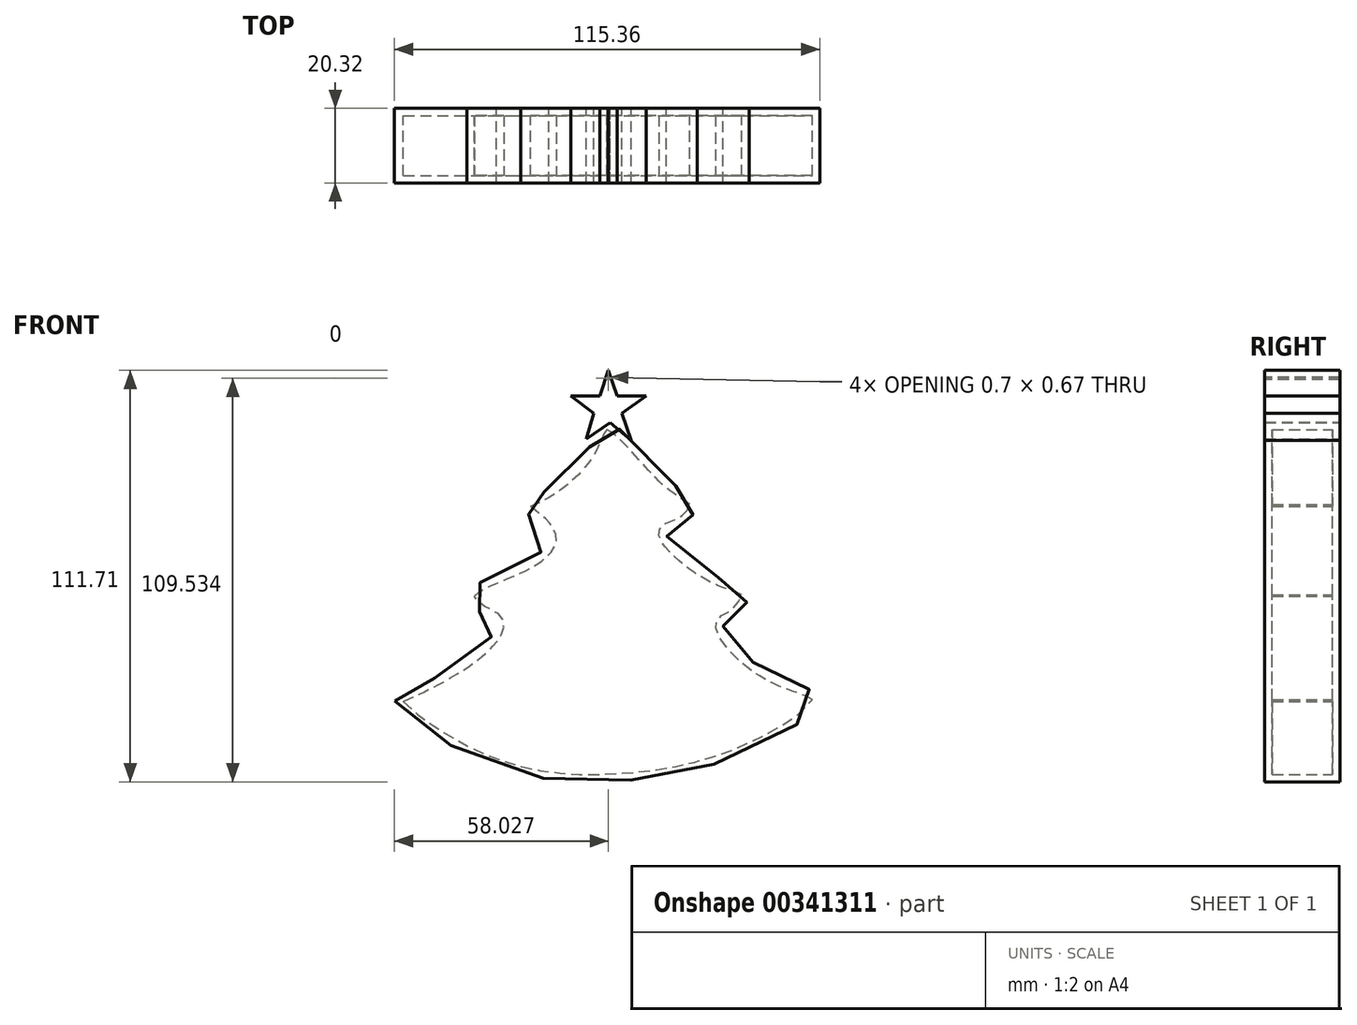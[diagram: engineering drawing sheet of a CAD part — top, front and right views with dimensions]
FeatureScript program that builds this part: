
annotation { "Feature Type Name" : "Feature", "Feature Type Description" : "" }
export const myFeature = defineFeature(function(context is Context, id is Id, definition is map)
    precondition{}
    {
        {
            var Q0;
            Q0=qCreatedBy(makeId("Front.planeOp"),FACE);
            var sketch = newSketch(context, id + "F0", { "sketchPlane" : qUnion([Q0])});
            skPoint(sketch, "E0.15.internal.snap0", {"position": v(1.13, 56.39) * mm});
            skFitSpline(sketch, "E0", {"points": [v(-56.53, -29.1) * mm, v(-32.06, -45.7) * mm, v(5.35, -50.76) * mm, v(39.1, -42.89) * mm, v(58.79, -28.54) * mm, v(48.38, -23.2) * mm, v(35.16, -13.36) * mm, v(32.63, -8.3) * mm, v(35.16, -6.6) * mm, v(39.66, 0) * mm, v(30.1, 4.92) * mm, v(17.16, 16.45) * mm, v(20.82, 18.42) * mm, v(25.6, 24.33) * mm, v(18.85, 29.95) * mm, v(1.13, 46.54) * mm, v(-4.21, 38.67) * mm, v(-18, 26.58) * mm, v(-22.21, 23.76) * mm, v(-14.9, 16.17) * mm, v(-21.93, 8.02) * mm, v(-36.84, 0) * mm, v(-33.46, -4.92) * mm, v(-28.96, -8.02) * mm, v(-34.87, -16.17) * mm, v(-54.28, -27.14) * mm, v(-56.53, -29.1) * mm]});
            skSolve(sketch);
        }
        {
            var Q0;
            Q0 = qSketchRegion(id + "F0", true);
            extrude(context, id + "F1", {"entities" : qUnion([Q0]), "depth" : 20.32 * mm});
        }
        {
            var Q0;
            Q0=makeQuery(id+"F1.opExtrude","CAP_FACE",FACE,{"disambiguationData":[OSD([sQuery(id+"F0.wireOp",EDGE,"E0")])],"isStart":false});
            var Q1;
            Q1=makeQuery(id+"F1.opExtrude","SWEPT_BODY",BODY,{"disambiguationData":[OSD([sQuery(id+"F0.wireOp",EDGE,"E0")])]});
            shell(context, id + "F2", {"isHollow" : true, "entities" : qUnion([Q0]), "parts" : qUnion([Q1]), "thickness" : 2 * mm});
        }
        {
            var Q0;
            Q0=makeQuery(id+"F1.opExtrude","CAP_FACE",FACE,{"disambiguationData":[OSD([sQuery(id+"F0.wireOp",EDGE,"E0")])],"isStart":false});
            var sketch = newSketch(context, id + "F3", { "sketchPlane" : qUnion([Q0])});
            skLineSegment(sketch, "E1", {"start": v(-8.68, 53.61) * mm, "end": v(-0.89, 53.61) * mm});
            skLineSegment(sketch, "E2", {"start": v(-0.89, 53.61) * mm, "end": v(1.45, 60.62) * mm});
            skLineSegment(sketch, "E3", {"start": v(1.45, 60.62) * mm, "end": v(3.86, 53.7) * mm});
            skLineSegment(sketch, "E4", {"start": v(3.86, 53.7) * mm, "end": v(11.75, 53.7) * mm});
            skLineSegment(sketch, "E5", {"start": v(11.75, 53.7) * mm, "end": v(5.18, 48.94) * mm});
            skLineSegment(sketch, "E6", {"start": v(5.18, 48.94) * mm, "end": v(7.65, 41.6) * mm});
            skLineSegment(sketch, "E7", {"start": v(7.65, 41.6) * mm, "end": v(1.9, 46.37) * mm});
            skLineSegment(sketch, "E8", {"start": v(1.9, 46.37) * mm, "end": v(-4.57, 42) * mm});
            skLineSegment(sketch, "E9", {"start": v(-4.57, 42) * mm, "end": v(-2.54, 48.94) * mm});
            skLineSegment(sketch, "E10", {"start": v(-2.54, 48.94) * mm, "end": v(-8.68, 53.61) * mm});
            skSolve(sketch);
        }
        {
            var Q0;
            Q0 = qSketchRegion(id + "F3", true);
            extrude(context, id + "F4", {"entities" : qUnion([Q0]), "depth" : 20.32 * mm});
        }
        {
            var Q0;
            Q0=makeQuery(id+"F4.opExtrude","SWEPT_BODY",BODY,{"disambiguationData":[OSD([sQuery(id+"F3.wireOp",EDGE,"E1"),sQuery(id+"F3.wireOp",EDGE,"E2"),sQuery(id+"F3.wireOp",EDGE,"E3"),sQuery(id+"F3.wireOp",EDGE,"E4"),sQuery(id+"F3.wireOp",EDGE,"E5"),sQuery(id+"F3.wireOp",EDGE,"E6"),sQuery(id+"F3.wireOp",EDGE,"E7"),sQuery(id+"F3.wireOp",EDGE,"E8"),sQuery(id+"F3.wireOp",EDGE,"E9"),sQuery(id+"F3.wireOp",EDGE,"E10")])]});
            var Q1;
            Q1=makeQuery(id+"F4.opExtrude","SWEPT_EDGE",EDGE,{"disambiguationData":[OSD([sQuery(id+"F0.wireOp",EDGE,"E0"),sQuery(id+"F3.wireOp",EDGE,"E6"),sQuery(id+"F3.wireOp",EDGE,"E7")])]});
            transform(context, id + "F5", {"entities" : qUnion([Q0]), "transformType" : TransformType.TRANSLATION_ENTITY, "oppositeDirectionEntity" : false, "transformLine" : qUnion([Q1]), "makeCopy" : false});
        }
        {
            var Q0;
            Q0=makeQuery(id+"F4.opExtrude","CAP_FACE",FACE,{"disambiguationData":[OSD([sQuery(id+"F3.wireOp",EDGE,"E1"),sQuery(id+"F3.wireOp",EDGE,"E2"),sQuery(id+"F3.wireOp",EDGE,"E3"),sQuery(id+"F3.wireOp",EDGE,"E4"),sQuery(id+"F3.wireOp",EDGE,"E5"),sQuery(id+"F3.wireOp",EDGE,"E6"),sQuery(id+"F3.wireOp",EDGE,"E7"),sQuery(id+"F3.wireOp",EDGE,"E8"),sQuery(id+"F3.wireOp",EDGE,"E9"),sQuery(id+"F3.wireOp",EDGE,"E10")])],"isStart":false});
            var sketch = newSketch(context, id + "F6", { "sketchPlane" : qUnion([Q0])});
            skLineSegment(sketch, "E11", {"start": v(1.12, 58.52) * mm, "end": v(1.38, 58.52) * mm});
            skLineSegment(sketch, "E12", {"start": v(1.38, 58.52) * mm, "end": v(1.46, 58.78) * mm});
            skLineSegment(sketch, "E13", {"start": v(1.46, 58.78) * mm, "end": v(1.54, 58.52) * mm});
            skLineSegment(sketch, "E14", {"start": v(1.54, 58.52) * mm, "end": v(1.82, 58.52) * mm});
            skLineSegment(sketch, "E15", {"start": v(1.82, 58.52) * mm, "end": v(1.6, 58.37) * mm});
            skLineSegment(sketch, "E16", {"start": v(1.6, 58.37) * mm, "end": v(1.68, 58.1) * mm});
            skLineSegment(sketch, "E17", {"start": v(1.68, 58.1) * mm, "end": v(1.46, 58.26) * mm});
            skLineSegment(sketch, "E18", {"start": v(1.46, 58.26) * mm, "end": v(1.24, 58.1) * mm});
            skLineSegment(sketch, "E19", {"start": v(1.24, 58.1) * mm, "end": v(1.32, 58.36) * mm});
            skLineSegment(sketch, "E20", {"start": v(1.32, 58.36) * mm, "end": v(1.12, 58.52) * mm});
            skSolve(sketch);
        }
        {
            var Q0;
            Q0 = qSketchRegion(id + "F6", true);
            extrude(context, id + "F7", {"entities" : qUnion([Q0]), "operationType" : NewBodyOperationType.REMOVE, "oppositeDirection" : true, "depth" : 25.4 * mm});
        }
    });
